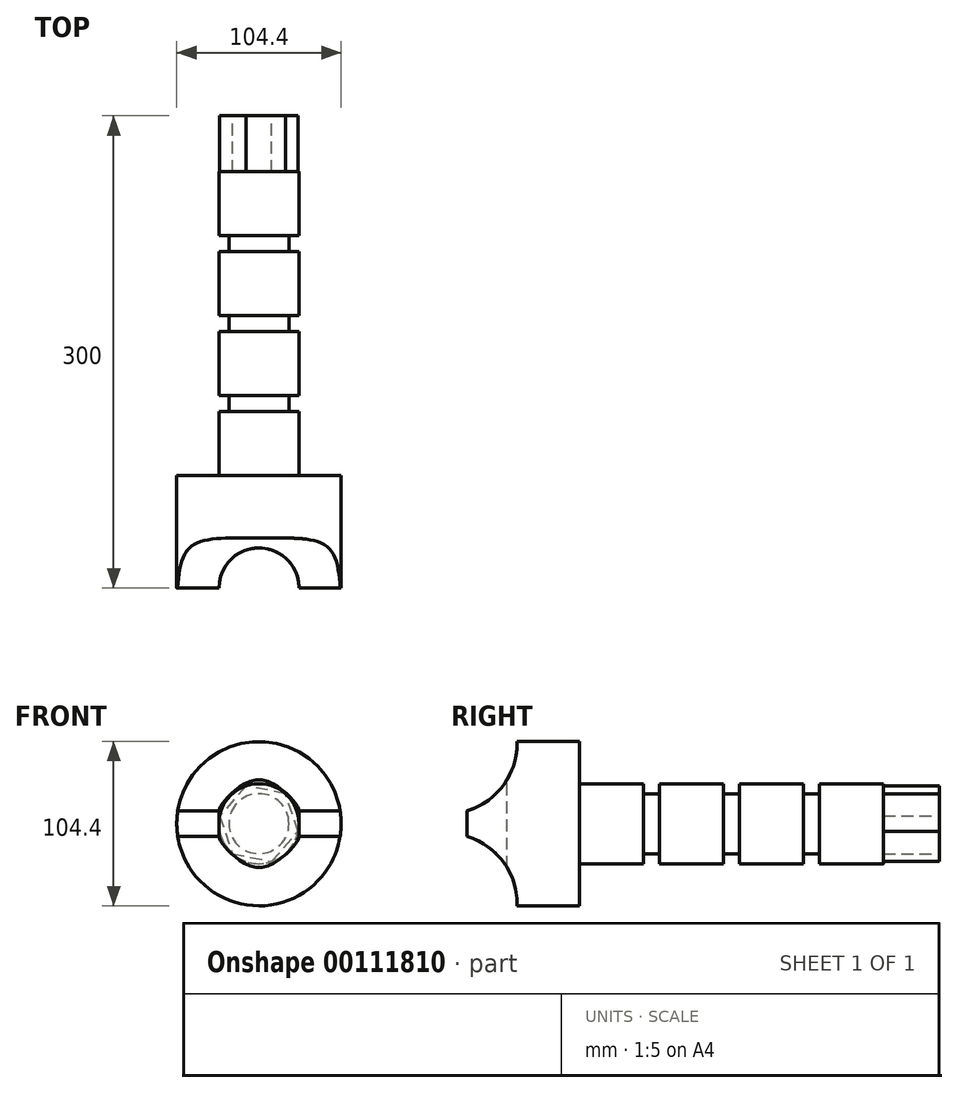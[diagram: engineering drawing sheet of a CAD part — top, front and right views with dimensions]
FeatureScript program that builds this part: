
annotation { "Feature Type Name" : "Feature", "Feature Type Description" : "" }
export const myFeature = defineFeature(function(context is Context, id is Id, definition is map)
    precondition{}
    {
        {
            var Q0;
            Q0=qCreatedBy(makeId("Front.planeOp"),FACE);
            var sketch = newSketch(context, id + "F0", { "sketchPlane" : qUnion([Q0])});
            skCircle(sketch, "E0", {"center": v(0, 0) * mm, "radius": 52.2 * mm});
            skSolve(sketch);
        }
        {
            var Q0;
            Q0=makeQuery(id+"F0.imprint","IMPRINT",FACE,{"disambiguationData":[TD([[makeQuery(id+"F0.imprint","IMPRINT",EDGE,{"derivedFrom":sQuery(id+"F0.wireOp",EDGE,"E0")}),1.0]])]});
            extrude(context, id + "F1", {"entities" : qUnion([Q0]), "oppositeDirection" : true, "depth" : 300 * mm});
        }
        {
            var Q0;
            Q0=qCreatedBy(makeId("Top.planeOp"),FACE);
            cPlane(context, id + "F2", {"entities" : qUnion([Q0]), "cplaneType" : CPlaneType.OFFSET, "offset" : 63.5 * mm, "width" : 152.4 * mm, "height" : 152.4 * mm});
        }
        {
            var Q0;
            Q0=qCreatedBy(id+"F2.planeOp",FACE);
            var sketch = newSketch(context, id + "F3", { "sketchPlane" : qUnion([Q0])});
            skCircle(sketch, "E1", {"center": v(0, 0) * mm, "radius": 25.4 * mm});
            skSolve(sketch);
        }
        {
            var Q0;
            Q0=makeQuery(id+"F3.imprint","IMPRINT",FACE,{"disambiguationData":[TD([[makeQuery(id+"F3.imprint","IMPRINT",EDGE,{"derivedFrom":sQuery(id+"F3.wireOp",EDGE,"E1")}),1.0]])]});
            extrude(context, id + "F4", {"entities" : qUnion([Q0]), "operationType" : NewBodyOperationType.REMOVE, "oppositeDirection" : true, "depth" : 152.4 * mm});
        }
        {
            var Q0;
            Q0=qCreatedBy(makeId("Right.planeOp"),FACE);
            cPlane(context, id + "F5", {"entities" : qUnion([Q0]), "cplaneType" : CPlaneType.OFFSET, "offset" : 63.5 * mm, "width" : 152.4 * mm, "height" : 152.4 * mm});
        }
        {
            var Q0;
            Q0=qCreatedBy(id+"F5.planeOp",FACE);
            var sketch = newSketch(context, id + "F6", { "sketchPlane" : qUnion([Q0])});
            skPoint(sketch, "E2", {"position": v(-12.7, 50.8) * mm});
            skPoint(sketch, "E3", {"position": v(-12.7, -50.8) * mm});
            skCircle(sketch, "E4", {"center": v(-12.7, 50.8) * mm, "radius": 44.45 * mm});
            skCircle(sketch, "E5", {"center": v(-12.7, -50.8) * mm, "radius": 44.45 * mm});
            skSolve(sketch);
        }
        {
            var Q0;
            Q0=makeQuery(id+"F6.imprint","IMPRINT",FACE,{"disambiguationData":[TD([[makeQuery(id+"F6.imprint","IMPRINT",EDGE,{"derivedFrom":sQuery(id+"F6.wireOp",EDGE,"E5")}),1.0]])]});
            var Q1;
            Q1=makeQuery(id+"F6.imprint","IMPRINT",FACE,{"disambiguationData":[TD([[makeQuery(id+"F6.imprint","IMPRINT",EDGE,{"derivedFrom":sQuery(id+"F6.wireOp",EDGE,"E4")}),1.0]])]});
            extrude(context, id + "F7", {"entities" : qUnion([Q0, Q1]), "operationType" : NewBodyOperationType.REMOVE, "oppositeDirection" : true, "depth" : 152.4 * mm});
        }
        {
            var Q0;
            Q0=makeQuery(id+"F1.opExtrude","CAP_FACE",FACE,{"disambiguationData":[OSD([sQuery(id+"F0.wireOp",EDGE,"E0")])],"isStart":false});
            var sketch = newSketch(context, id + "F8", { "sketchPlane" : qUnion([Q0])});
            skCircle(sketch, "E6", {"center": v(0, 0) * mm, "radius": 25.4 * mm});
            skSolve(sketch);
        }
        {
            var Q0;
            Q0=makeQuery(id+"F8.imprint","IMPRINT",FACE,{"disambiguationData":[TD([[makeQuery(id+"F8.imprint","IMPRINT",EDGE,{"derivedFrom":sQuery(id+"F8.wireOp",EDGE,"E6")}),-1.0]])]});
            extrude(context, id + "F9", {"entities" : qUnion([Q0]), "operationType" : NewBodyOperationType.REMOVE, "oppositeDirection" : true, "depth" : 228.6 * mm});
        }
        {
            var Q0;
            Q0=makeQuery(id+"F9.boolean.opBoolean","COPY",FACE,{"derivedFrom":makeQuery(id+"F9.opExtrude","CAP_FACE",FACE,{"disambiguationData":[OSD([sQuery(id+"F0.wireOp",EDGE,"E0"),sQuery(id+"F8.wireOp",EDGE,"E6")])],"isStart":false})});
            cPlane(context, id + "F10", {"entities" : qUnion([Q0]), "cplaneType" : CPlaneType.OFFSET, "offset" : 50.8 * mm, "width" : 152.4 * mm, "height" : 152.4 * mm});
        }
        {
            var Q0;
            Q0=qCreatedBy(id+"F10.planeOp",FACE);
            cPlane(context, id + "F11", {"entities" : qUnion([Q0]), "cplaneType" : CPlaneType.OFFSET, "offset" : 50.8 * mm, "width" : 152.4 * mm, "height" : 152.4 * mm});
        }
        {
            var Q0;
            Q0=qCreatedBy(id+"F11.planeOp",FACE);
            cPlane(context, id + "F12", {"entities" : qUnion([Q0]), "cplaneType" : CPlaneType.OFFSET, "offset" : 50.8 * mm, "width" : 152.4 * mm, "height" : 152.4 * mm});
        }
        {
            var Q0;
            Q0=qCreatedBy(id+"F10.planeOp",FACE);
            var sketch = newSketch(context, id + "F13", { "sketchPlane" : qUnion([Q0])});
            skCircle(sketch, "E7", {"center": v(0, 0) * mm, "radius": 19.05 * mm});
            skCircle(sketch, "E8", {"center": v(0, 0) * mm, "radius": 31.75 * mm});
            skSolve(sketch);
        }
        {
            var Q0;
            Q0=qCreatedBy(id+"F12.planeOp",FACE);
            var sketch = newSketch(context, id + "F14", { "sketchPlane" : qUnion([Q0])});
            skCircle(sketch, "E9", {"center": v(0, 0) * mm, "radius": 31.75 * mm});
            skCircle(sketch, "E10", {"center": v(0, 0) * mm, "radius": 19.05 * mm});
            skSolve(sketch);
        }
        {
            var Q0;
            Q0=qCreatedBy(id+"F11.planeOp",FACE);
            var sketch = newSketch(context, id + "F15", { "sketchPlane" : qUnion([Q0])});
            skCircle(sketch, "E11", {"center": v(0, 0) * mm, "radius": 31.75 * mm});
            skCircle(sketch, "E12", {"center": v(0, 0) * mm, "radius": 19.05 * mm});
            skSolve(sketch);
        }
        {
            var Q0;
            Q0=makeQuery(id+"F13.imprint","IMPRINT",FACE,{"disambiguationData":[TD([[makeQuery(id+"F13.imprint","IMPRINT",EDGE,{"derivedFrom":sQuery(id+"F13.wireOp",EDGE,"E7")}),-1.0]])]});
            var Q1;
            Q1=makeQuery(id+"F15.imprint","IMPRINT",FACE,{"disambiguationData":[TD([[makeQuery(id+"F15.imprint","IMPRINT",EDGE,{"derivedFrom":sQuery(id+"F15.wireOp",EDGE,"E11")}),1.0]])]});
            var Q2;
            Q2=makeQuery(id+"F14.imprint","IMPRINT",FACE,{"disambiguationData":[TD([[makeQuery(id+"F14.imprint","IMPRINT",EDGE,{"derivedFrom":sQuery(id+"F14.wireOp",EDGE,"E9")}),1.0]])]});
            extrude(context, id + "F16", {"entities" : qUnion([Q0, Q1, Q2]), "operationType" : NewBodyOperationType.REMOVE, "oppositeDirection" : true, "depth" : 10.16 * mm});
        }
        {
            var Q0;
            Q0=makeQuery(id+"F1.opExtrude","CAP_FACE",FACE,{"disambiguationData":[OSD([sQuery(id+"F0.wireOp",EDGE,"E0")])],"isStart":false});
            var sketch = newSketch(context, id + "F17", { "sketchPlane" : qUnion([Q0])});
            skCircle(sketch, "E13", {"center": v(0, 0) * mm, "radius": 25.4 * mm});
            skCircle(sketch, "E14.cCircle", {"center": v(0, 0) * mm, "radius": 25.4 * mm, "construction": true});
            skLineSegment(sketch, "E14.0", {"start": v(-24.9, -5.02) * mm, "end": v(-16.8, 19.05) * mm});
            skLineSegment(sketch, "E14.1", {"start": v(-16.8, 19.05) * mm, "end": v(8.1, 24.07) * mm});
            skLineSegment(sketch, "E14.2", {"start": v(8.1, 24.07) * mm, "end": v(24.9, 5.02) * mm});
            skLineSegment(sketch, "E14.3", {"start": v(24.9, 5.02) * mm, "end": v(16.8, -19.05) * mm});
            skLineSegment(sketch, "E14.4", {"start": v(16.8, -19.05) * mm, "end": v(-8.1, -24.07) * mm});
            skLineSegment(sketch, "E14.5", {"start": v(-8.1, -24.07) * mm, "end": v(-24.9, -5.02) * mm});
            skSolve(sketch);
        }
        {
            var Q0;
            {var subQ0=sQuery(id+"F17.wireOp",EDGE,"E14.0");Q0=makeQuery(id+"F17.imprint","IMPRINT",FACE,{"disambiguationData":[TD([[makeQuery(id+"F17.imprint","IMPRINT",EDGE,{"derivedFrom":subQ0}),1.0]])]});}
            var Q1;
            {var subQ0=sQuery(id+"F17.wireOp",EDGE,"E14.1");Q1=makeQuery(id+"F17.imprint","IMPRINT",FACE,{"disambiguationData":[TD([[makeQuery(id+"F17.imprint","IMPRINT",EDGE,{"derivedFrom":subQ0}),1.0]])]});}
            var Q2;
            {var subQ0=sQuery(id+"F17.wireOp",EDGE,"E14.2");Q2=makeQuery(id+"F17.imprint","IMPRINT",FACE,{"disambiguationData":[TD([[makeQuery(id+"F17.imprint","IMPRINT",EDGE,{"derivedFrom":subQ0}),1.0]])]});}
            var Q3;
            {var subQ0=sQuery(id+"F17.wireOp",EDGE,"E14.3");Q3=makeQuery(id+"F17.imprint","IMPRINT",FACE,{"disambiguationData":[TD([[makeQuery(id+"F17.imprint","IMPRINT",EDGE,{"derivedFrom":subQ0}),1.0]])]});}
            var Q4;
            {var subQ0=sQuery(id+"F17.wireOp",EDGE,"E14.4");Q4=makeQuery(id+"F17.imprint","IMPRINT",FACE,{"disambiguationData":[TD([[makeQuery(id+"F17.imprint","IMPRINT",EDGE,{"derivedFrom":subQ0}),1.0]])]});}
            var Q5;
            {var subQ0=sQuery(id+"F17.wireOp",EDGE,"E14.5");Q5=makeQuery(id+"F17.imprint","IMPRINT",FACE,{"disambiguationData":[TD([[makeQuery(id+"F17.imprint","IMPRINT",EDGE,{"derivedFrom":subQ0}),1.0]])]});}
            extrude(context, id + "F18", {"entities" : qUnion([Q0, Q1, Q2, Q3, Q4, Q5]), "operationType" : NewBodyOperationType.REMOVE, "oppositeDirection" : true, "depth" : 35.56 * mm});
        }
    });
